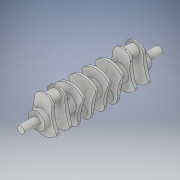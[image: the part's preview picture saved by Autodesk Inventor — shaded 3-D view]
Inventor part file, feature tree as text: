
AUTODESK INVENTOR PART (.ipt)
format: ipt  version: 2018 (Build 220112000, 112)  size: 522,240 bytes
history: native  units: in
note: dims shown in document units (in); Inventor stores cm internally (conversion verified against a paired STEP export)
features: extrude x17, sketch x16, plane x9, projected_geometry x6, loft x4, other x4, fillet x3, mirror x2
ambient origin geometry x8: Origin, YZ Plane, XZ Plane, XY Plane, X Axis, Y Axis, Z Axis, Center Point
bodies: Solid1 (feature_tree)
feature tree (61):
  extrude  "Extrusion1"  Depth=2.0in TaperAngle=0.0deg
  extrude  "Extrusion2"  Depth=1.0in TaperAngle=0.0deg
  plane  "Work Plane1"
  plane  "Work Plane2"
  sketch  "Sketch3"  dims[d6=0.25in d7=0.5in]
  loft  "Loft1"
  extrude  "Extrusion3"  TaperAngle=0.0deg  [1 undecoded]
  extrude  "Extrusion4"  Depth=0.25in TaperAngle=0.0deg
  extrude  "Extrusion5"  Depth=1.85in
  plane  "Work Plane3"
  sketch  "Sketch6"  dims[d15=1.5in d16=1.85in]
  loft  "Loft2"
  extrude  "Extrusion6"  TaperAngle=0.0deg  [1 undecoded]
  plane  "Work Plane4"
  sketch  "Sketch7"  dims[d17=1.5in d18=0.0in d19=0.25in d20=0.0in]
  loft  "Loft3"
  extrude  "Extrusion7"  Depth=0.25in
  extrude  "Extrusion8"  TaperAngle=0.0deg  [1 undecoded]
  extrude  "Extrusion9"  Depth=0.25in
  fillet  "Fillet1"  Radius=1.85in
  extrude  "Extrusion10"  Depth=4.5in TaperAngle=0.0deg
  plane  "Work Plane5"
  loft  "Loft4"
  extrude  "Extrusion11"  Depth=0.3138in
  extrude  "Extrusion12"  Depth=0.25in TaperAngle=0.0deg
  fillet  "Fillet2"  Radius=0.25in
  fillet  "Fillet3"  [1 undecoded]
  mirror  "Mirror1"
  extrude  "Extrusion13"  TaperAngle=0.0deg  [1 undecoded]
  plane  "Work Plane8"
  mirror  "Mirror2"
  extrude  "Extrusion14"  Depth=0.25in TaperAngle=0.0deg
  plane  "Work Plane9"
  sketch  "Sketch16"  dims[d44=6.0in d45=0.3138in]
  extrude  "Extrusion15"  Depth=0.25in
  extrude  "Extrusion16"  Depth=0.25in
  extrude  "Extrusion17"  Depth=0.25in
  sketch  "Sketch1"  dims[d0=1.0in d1=2.0in d2=0.0in]
  sketch  "Sketch2"  dims[d3=2.36in d4=1.0in d5=0.0in]
  other  "Edges1"
  sketch  "Sketch4"  dims[d8=5.7in d9=0.0in d10=90.0deg]
  sketch  "Sketch5"  dims[d11=0.0in d12=90.0deg d13=0.25in d14=0.0in]
  other  "Edges2"
  other  "Edges3"
  sketch  "Sketch8"  dims[d21=0.25in d22=0.0in d23=90.0deg]
  projected_geometry  "Projected Loop1"
  sketch  "Sketch10"  dims[d24=0.0in d25=90.0deg d26=1.2in d27=0.0in]
  sketch  "Sketch11"  dims[d28=0.25in d29=5.7in]
  projected_geometry  "Projected Loop2"
  other  "Edges4"
  sketch  "Sketch12"  dims[d30=0.0in d31=90.0deg d32=0.0in d33=90.0deg]
  projected_geometry  "Projected Loop3"
  sketch  "Sketch13"  dims[d34=0.25in d35=0.0in d36=1.5in d37=1.85in]
  projected_geometry  "Projected Loop4"
  plane  "Work Plane6"
  plane  "Work Plane7"
  sketch  "Sketch14"  dims[d38=1.5in d39=0.0in d40=4.5in d41=0.0in]
  projected_geometry  "Projected Loop5"
  sketch  "Sketch15"  dims[d42=1.3in d43=6.5in]
  projected_geometry  "Projected Loop6"
  sketch  "Sketch17"  dims[d46=1.0in d47=0.25in d48=0.0in d49=0.25in d50=0.0in d51=90.0deg d52=0.0in d53=90.0deg d54=0.6in d55=0.0in d56=6.5in d57=0.314in d58=6.0in d59=3.4in d60=3.4in d61=3.4in d62=0.0in d63=3.0in d64=0.0in d65=1.0in d66=0.25in d67=0.25in d68=0.0in d69=0.0in d70=2.5in d71=0.25in d72=0.25in d73=0.25in d74=4.0in d75=0.0in d76=0.0in d77=2.5in d78=0.25in d79=0.25in d80=5.0in d81=0.0in d82=2.0in d83=0.0in d84=180.0deg d85=2.5in d86=0.25in d87=0.25in d88=4.0in d89=0.0in]
note: 5 required parameter values undecoded (feature->parameter linkage not recoverable at this tier; creation-order binding heuristic only, values carry confidence <= 0.55)
